# Revit family: Lithium Swingblade Exit_Hosted_R18
name_source: partatom
category: Lighting Fixtures
revit_build: Autodesk Revit 2018 (Build: 20170223_1515(x64)
units: mm (PartAtom-declared; Revit-internal decimal feet)

## family parameters
Cut with Voids When Loaded = No
Host = Face
Light Source = Yes
Part Type = Normal
Room Calculation Point = No
Round Connector Dimension = Use Diameter
Shared = No

## types (1)
- LSBLED
    AS2293 = C0=D6.3 C90=E3.2
    Annotation Direction = Exit_Annotation : Double Sided Exit Luminaire
    Apparent Load = 5 W
    Ballast = Electronic
    Battery = P/N: 1530070, L10 3.3V 2.5AH
    Charging Method = Intelligent Current Limited Constant Voltage
    Color Filter = 16777215
    Default Elevation = 1219 mm
    Description = LED Premium Swingblade Exit
    Diffuser = All directional inserts included in the box
    Dimming Lamp Color Temperature Shift = <None>
    Emit Shape Visible in Rendering = No
    Emit from Circle Diameter = 435 mm
    Finish = White powder coated metal body and white plastic end caps
    Height = 263 mm
    Inverter Board = P/N: 8002355, PCA:Lithium S/BLADE Driver
    Lamp = P/N: 8002175, PCA:24DLED UB LED Strip
    Length = 435 mm
    Manufacturer = Clevertronics
    Model = ZSBLED-TH-DS-R
    Mounting = Surface Mount, Wall or Ceiling on a slide connect bracket - Single & Double Sided
Can also be suspended via 2 x Rods/Wire
    Operating Mode = Maintained
    Operating Voltage = 240 V
    Photometric Web File = Premium LED Swingblade Exit.ies
    Power Consumption = 6 W
    Sign Direction = Sign : Exit
    Testing System = Manual Test Switch
    Value = 2
    Viewing Distance = 24000 mm
    Wattage Comments = Standby
    Width = 90 mm  [stored 0.295276 ft]

note: [stored X ft] marks values corroborated as IEEE doubles in the binary element streams (Revit-internal decimal feet)

## geometry (parser evidence)
native form markers: Blend x2, Sweep x5
no freeform markers — native parametric forms only
